# Revit family: Kitchen_Sinks_hansgrohe_43453CHN-S43-S439-U400-Under-mount-sink_jgd
name_source: partatom
category: Plumbing Fixtures
revit_build: Autodesk Revit 2018 (Build: 20170223_1515(x64)
units: mm (PartAtom-declared; Revit-internal decimal feet)

## family parameters
Cut with Voids When Loaded = No
Host = Face
OmniClass Number = 23.31.13.00
OmniClass Title = Sinks
Part Type = Normal
Room Calculation Point = No
Round Connector Dimension = Use Diameter
Shared = No

## types (1)
- 807 Stainless Steel
    BIMobject category = Sinks
    Connector Description = Water Outlet 45 mm
    Default Elevation = 1219 mm
    Description = S43 S439-U400 Under-mount sink 400 incl. manual drain kit
    Design country = Germany
    Diameter = 45  [stored 0.147638 ft]
    Edition number = 1
    IFC Classification = Sanitary Terminal
    Manufacturer = Hansgrohe
    Manufacturer country = Germany
    Manufacturer name = hansgrohe
    Material = Hansgrohe - Metal - 807 Stainless Steel
    Material main = Stainless steel
    Model = 43453CHN
    OmniClass Code = 23-31 13 00
    OmniClass Description = Sinks
    Product Guid = 6af11be9-9a46-480f-b21b-6846841af423
    Product SKU = 43453CHN
    Product data url = https://bimobject.com
    Product family = S43
    Product group = Sinks
    Product name = 43453CHN S43 S439-U400 Under-mount sink 400 incl. manual drain kit
    Product url = https://www.hansgrohe.com
    QR code = https://bimobject.com
    UNSPSC Code = 30181504
    URL = https://www.hansgrohe.com
    Uniclass 2015 Code = Pr_40_20_96_45
    Uniclass 2015 Name = Kitchen sinks
    Weight Net (Kg) = 2.9

note: [stored X ft] marks values corroborated as IEEE doubles in the binary element streams (Revit-internal decimal feet)

## geometry (parser evidence)
native form markers: Sweep x5
no freeform markers — native parametric forms only
